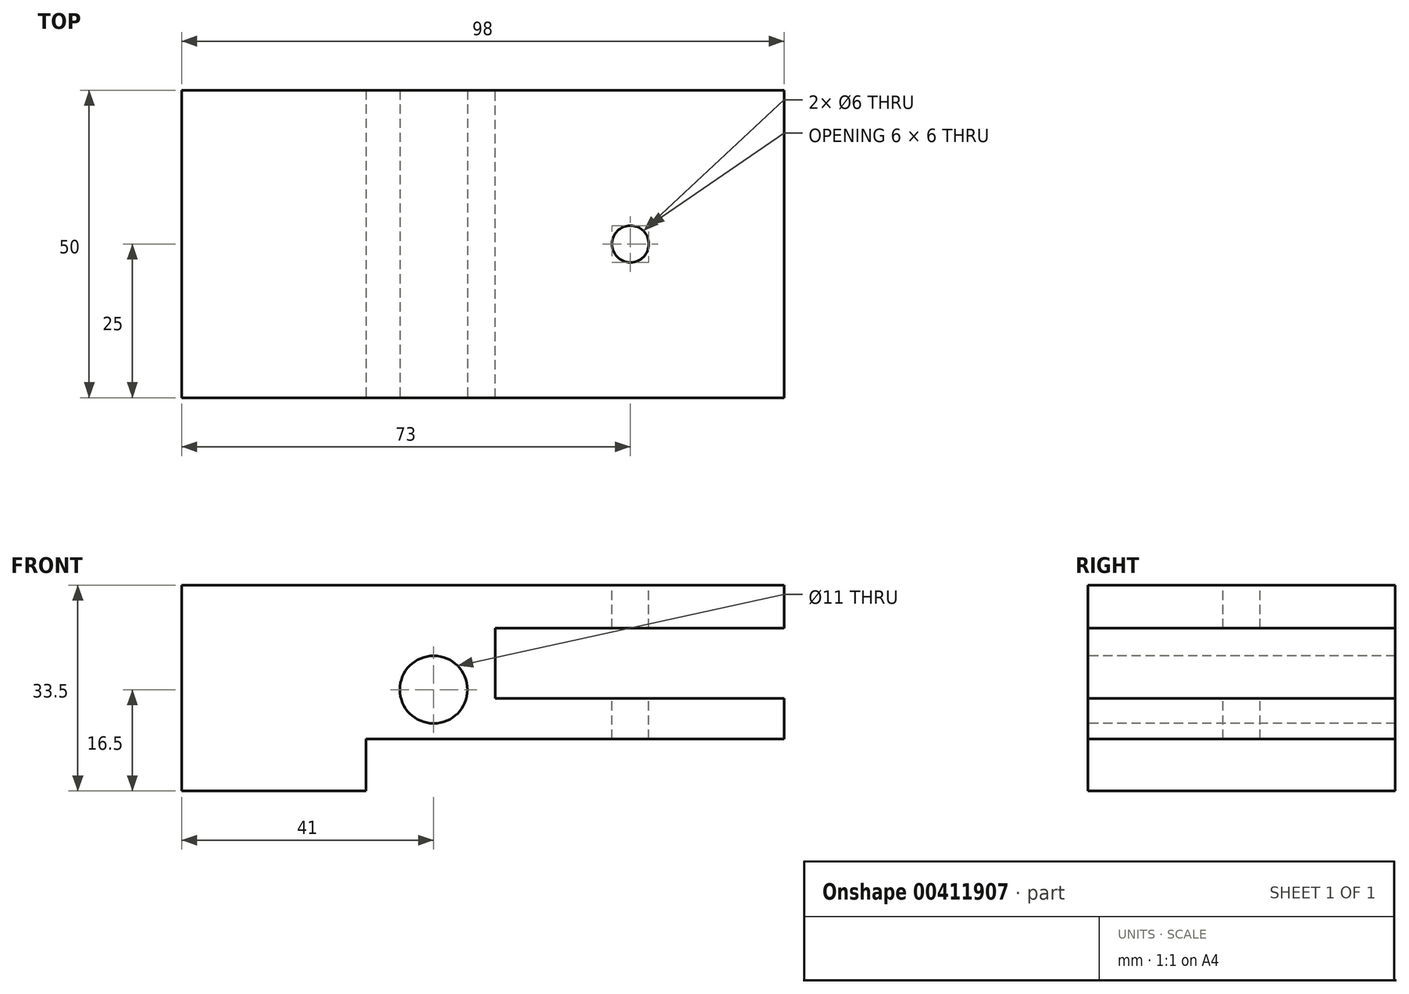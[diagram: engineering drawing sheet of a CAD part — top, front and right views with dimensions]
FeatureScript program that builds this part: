
annotation { "Feature Type Name" : "Feature", "Feature Type Description" : "" }
export const myFeature = defineFeature(function(context is Context, id is Id, definition is map)
    precondition{}
    {
        {
            var Q0;
            Q0=qCreatedBy(makeId("Front.planeOp"),FACE);
            var sketch = newSketch(context, id + "F0", { "sketchPlane" : qUnion([Q0])});
            skLineSegment(sketch, "E0.bottom", {"start": v(-183, 33.5) * mm, "end": v(183, 33.5) * mm});
            skLineSegment(sketch, "E0.top", {"start": v(-183, 0) * mm, "end": v(183, 0) * mm});
            skLineSegment(sketch, "E0.left", {"start": v(-183, 33.5) * mm, "end": v(-183, 0) * mm});
            skLineSegment(sketch, "E0.right", {"start": v(183, 33.5) * mm, "end": v(183, 0) * mm});
            skSolve(sketch);
        }
        {
            var Q0;
            Q0=makeQuery(id+"F0.imprint","IMPRINT",FACE,{"disambiguationData":[TD([[makeQuery(id+"F0.imprint","IMPRINT",EDGE,{"derivedFrom":sQuery(id+"F0.wireOp",EDGE,"E0.bottom")}),-1.0]])]});
            extrude(context, id + "F1", {"entities" : qUnion([Q0]), "endBound" : BoundingType.SYMMETRIC, "depth" : 50 * mm});
        }
        {
            var Q0;
            Q0=makeQuery(id+"F1.opExtrude","SWEPT_FACE",FACE,{"disambiguationData":[OSD([sQuery(id+"F0.wireOp",EDGE,"E0.right")])]});
            var sketch = newSketch(context, id + "F2", { "sketchPlane" : qUnion([Q0])});
            skLineSegment(sketch, "E1.bottom", {"start": v(-25, 26.5) * mm, "end": v(25, 26.5) * mm});
            skLineSegment(sketch, "E1.top", {"start": v(-25, 15.1) * mm, "end": v(25, 15.1) * mm});
            skLineSegment(sketch, "E1.left", {"start": v(-25, 26.5) * mm, "end": v(-25, 15.1) * mm});
            skLineSegment(sketch, "E1.right", {"start": v(25, 26.5) * mm, "end": v(25, 15.1) * mm});
            skSolve(sketch);
        }
        {
            var Q0;
            Q0=makeQuery(id+"F2.imprint","IMPRINT",FACE,{"disambiguationData":[TD([[makeQuery(id+"F2.imprint","IMPRINT",EDGE,{"derivedFrom":sQuery(id+"F2.wireOp",EDGE,"E1.bottom")}),-1.0]])]});
            extrude(context, id + "F3", {"entities" : qUnion([Q0]), "operationType" : NewBodyOperationType.REMOVE, "oppositeDirection" : true, "depth" : 47 * mm});
        }
        {
            var Q0;
            Q0=makeQuery(id+"F1.opExtrude","SWEPT_FACE",FACE,{"disambiguationData":[OSD([sQuery(id+"F0.wireOp",EDGE,"E0.left")])]});
            var sketch = newSketch(context, id + "F4", { "sketchPlane" : qUnion([Q0])});
            skLineSegment(sketch, "E2.bottom", {"start": v(-25, 26.5) * mm, "end": v(25, 26.5) * mm});
            skLineSegment(sketch, "E2.top", {"start": v(-25, 15.1) * mm, "end": v(25, 15.1) * mm});
            skLineSegment(sketch, "E2.left", {"start": v(-25, 26.5) * mm, "end": v(-25, 15.1) * mm});
            skLineSegment(sketch, "E2.right", {"start": v(25, 26.5) * mm, "end": v(25, 15.1) * mm});
            skSolve(sketch);
        }
        {
            var Q0;
            Q0=makeQuery(id+"F4.imprint","IMPRINT",FACE,{"disambiguationData":[TD([[makeQuery(id+"F4.imprint","IMPRINT",EDGE,{"derivedFrom":sQuery(id+"F4.wireOp",EDGE,"E2.bottom")}),-1.0]])]});
            extrude(context, id + "F5", {"entities" : qUnion([Q0]), "operationType" : NewBodyOperationType.REMOVE, "oppositeDirection" : true, "depth" : 53 * mm});
        }
        {
            var Q0;
            Q0=makeQuery(id+"F1.opExtrude","CAP_FACE",FACE,{"disambiguationData":[OSD([sQuery(id+"F0.wireOp",EDGE,"E0.bottom"),sQuery(id+"F0.wireOp",EDGE,"E0.top"),sQuery(id+"F0.wireOp",EDGE,"E0.left"),sQuery(id+"F0.wireOp",EDGE,"E0.right")])],"isStart":false});
            var sketch = newSketch(context, id + "F6", { "sketchPlane" : qUnion([Q0])});
            skLineSegment(sketch, "E3.bottom", {"start": v(183, 0) * mm, "end": v(115, 0) * mm});
            skLineSegment(sketch, "E3.top", {"start": v(183, 8.5) * mm, "end": v(115, 8.5) * mm});
            skLineSegment(sketch, "E3.left", {"start": v(183, 0) * mm, "end": v(183, 8.5) * mm});
            skLineSegment(sketch, "E3.right", {"start": v(115, 0) * mm, "end": v(115, 8.5) * mm});
            skLineSegment(sketch, "E4.bottom", {"start": v(-183, 0) * mm, "end": v(-115, 0) * mm});
            skLineSegment(sketch, "E4.top", {"start": v(-183, 8.5) * mm, "end": v(-115, 8.5) * mm});
            skLineSegment(sketch, "E4.left", {"start": v(-183, 0) * mm, "end": v(-183, 8.5) * mm});
            skLineSegment(sketch, "E4.right", {"start": v(-115, 0) * mm, "end": v(-115, 8.5) * mm});
            skSolve(sketch);
        }
        {
            var Q0;
            Q0=makeQuery(id+"F6.imprint","IMPRINT",FACE,{"disambiguationData":[TD([[makeQuery(id+"F6.imprint","IMPRINT",EDGE,{"derivedFrom":sQuery(id+"F6.wireOp",EDGE,"E4.bottom")}),1.0]])]});
            var Q1;
            Q1=makeQuery(id+"F6.imprint","IMPRINT",FACE,{"disambiguationData":[TD([[makeQuery(id+"F6.imprint","IMPRINT",EDGE,{"derivedFrom":sQuery(id+"F6.wireOp",EDGE,"E3.bottom")}),1.0]])]});
            extrude(context, id + "F7", {"entities" : qUnion([Q0, Q1]), "operationType" : NewBodyOperationType.REMOVE, "oppositeDirection" : true, "depth" : 100 * mm});
        }
        {
            var Q0;
            Q0=makeQuery(id+"F1.opExtrude","CAP_FACE",FACE,{"disambiguationData":[OSD([sQuery(id+"F0.wireOp",EDGE,"E0.bottom"),sQuery(id+"F0.wireOp",EDGE,"E0.top"),sQuery(id+"F0.wireOp",EDGE,"E0.left"),sQuery(id+"F0.wireOp",EDGE,"E0.right")])],"isStart":false});
            var sketch = newSketch(context, id + "F8", { "sketchPlane" : qUnion([Q0])});
            skLineSegment(sketch, "E5.bottom", {"start": v(-85, 33.5) * mm, "end": v(85, 33.5) * mm});
            skLineSegment(sketch, "E5.top", {"start": v(-85, 12.5) * mm, "end": v(85, 12.5) * mm});
            skLineSegment(sketch, "E5.left", {"start": v(-85, 33.5) * mm, "end": v(-85, 12.5) * mm});
            skLineSegment(sketch, "E5.right", {"start": v(85, 33.5) * mm, "end": v(85, 12.5) * mm});
            skSolve(sketch);
        }
        {
            var Q0;
            Q0=makeQuery(id+"F8.imprint","IMPRINT",FACE,{"disambiguationData":[TD([[makeQuery(id+"F8.imprint","IMPRINT",EDGE,{"derivedFrom":sQuery(id+"F8.wireOp",EDGE,"E5.bottom")}),-1.0]])]});
            extrude(context, id + "F9", {"entities" : qUnion([Q0]), "operationType" : NewBodyOperationType.REMOVE, "oppositeDirection" : true, "depth" : 79.8 * mm});
        }
        {
            var Q0;
            Q0=makeQuery(id+"F9.boolean.opBoolean","COPY",FACE,{"derivedFrom":makeQuery(id+"F9.opExtrude","SWEPT_FACE",FACE,{"disambiguationData":[OSD([sQuery(id+"F8.wireOp",EDGE,"E5.top")])]})});
            var sketch = newSketch(context, id + "F10", { "sketchPlane" : qUnion([Q0])});
            skCircle(sketch, "E6", {"center": v(0, 0) * mm, "radius": 11.5 * mm});
            skSolve(sketch);
        }
        {
            var Q0;
            Q0=makeQuery(id+"F10.imprint","IMPRINT",FACE,{"disambiguationData":[TD([[makeQuery(id+"F10.imprint","IMPRINT",EDGE,{"derivedFrom":sQuery(id+"F10.wireOp",EDGE,"E6")}),1.0]])]});
            extrude(context, id + "F11", {"entities" : qUnion([Q0]), "operationType" : NewBodyOperationType.REMOVE, "oppositeDirection" : true, "depth" : 56 * mm});
        }
        {
            var Q0;
            Q0=makeQuery(id+"F9.boolean.opBoolean","COPY",FACE,{"derivedFrom":makeQuery(id+"F9.opExtrude","SWEPT_FACE",FACE,{"disambiguationData":[OSD([sQuery(id+"F8.wireOp",EDGE,"E5.right")])]})});
            var sketch = newSketch(context, id + "F12", { "sketchPlane" : qUnion([Q0])});
            skLineSegment(sketch, "E7.bottom", {"start": v(39.14, -21) * mm, "end": v(-38.9, -21) * mm});
            skLineSegment(sketch, "E7.top", {"start": v(39.14, 51.1) * mm, "end": v(-38.9, 51.1) * mm});
            skLineSegment(sketch, "E7.left", {"start": v(39.14, -21) * mm, "end": v(39.14, 51.1) * mm});
            skLineSegment(sketch, "E7.right", {"start": v(-38.9, -21) * mm, "end": v(-38.9, 51.1) * mm});
            skSolve(sketch);
        }
        {
            var Q0;
            Q0 = qSketchRegion(id + "F12", true);
            extrude(context, id + "F13", {"entities" : qUnion([Q0]), "operationType" : NewBodyOperationType.REMOVE, "endBound" : BoundingType.UP_TO_NEXT, "depth" : 25 * mm});
        }
        {
            var Q0;
            {var subQ0=sQuery(id+"F0.wireOp",EDGE,"E0.right");var subQ3=sQuery(id+"F0.wireOp",EDGE,"E0.bottom");Q0=makeQuery(id+"F9.boolean.opBoolean","SPLIT",FACE,{"disambiguationData":[TD([makeQuery(id+"F1.opExtrude","SWEPT_FACE",FACE,{"disambiguationData":[OSD([subQ0])]})])],"derivedFrom":makeQuery(id+"F1.opExtrude","SWEPT_FACE",FACE,{"disambiguationData":[OSD([subQ3])]})});}
            var sketch = newSketch(context, id + "F14", { "sketchPlane" : qUnion([Q0])});
            skLineSegment(sketch, "E8.0.0", {"start": v(183, -25) * mm, "end": v(183, 25) * mm});
            skLineSegment(sketch, "E8.0.1", {"start": v(183, 25) * mm, "end": v(136, 25) * mm});
            skLineSegment(sketch, "E8.0.2", {"start": v(136, 25) * mm, "end": v(136, -25) * mm});
            skLineSegment(sketch, "E8.0.3", {"start": v(136, -25) * mm, "end": v(183, -25) * mm});
            skCircle(sketch, "E9", {"center": v(158, 0) * mm, "radius": 3 * mm});
            skSolve(sketch);
        }
        {
            var Q0;
            Q0=makeQuery(id+"F14.imprint","IMPRINT",FACE,{"disambiguationData":[TD([[makeQuery(id+"F14.imprint","IMPRINT",EDGE,{"derivedFrom":sQuery(id+"F14.wireOp",EDGE,"E9")}),1.0]])]});
            extrude(context, id + "F15", {"entities" : qUnion([Q0]), "operationType" : NewBodyOperationType.REMOVE, "oppositeDirection" : true, "depth" : 50 * mm});
        }
        {
            var Q0;
            Q0=makeQuery(id+"F8.imprint","IMPRINT",FACE,{"disambiguationData":[TD([[makeQuery(id+"F8.imprint","IMPRINT",EDGE,{"derivedFrom":sQuery(id+"F8.wireOp",EDGE,"E5.top")}),-1.0]])]});
            var sketch = newSketch(context, id + "F16", { "sketchPlane" : qUnion([Q0])});
            skCircle(sketch, "E10", {"center": v(126, 16.5) * mm, "radius": 5.5 * mm});
            skSolve(sketch);
        }
        {
            var Q0;
            Q0 = qSketchRegion(id + "F16", true);
            extrude(context, id + "F17", {"entities" : qUnion([Q0]), "operationType" : NewBodyOperationType.REMOVE, "oppositeDirection" : true, "depth" : 100 * mm});
        }
    });
